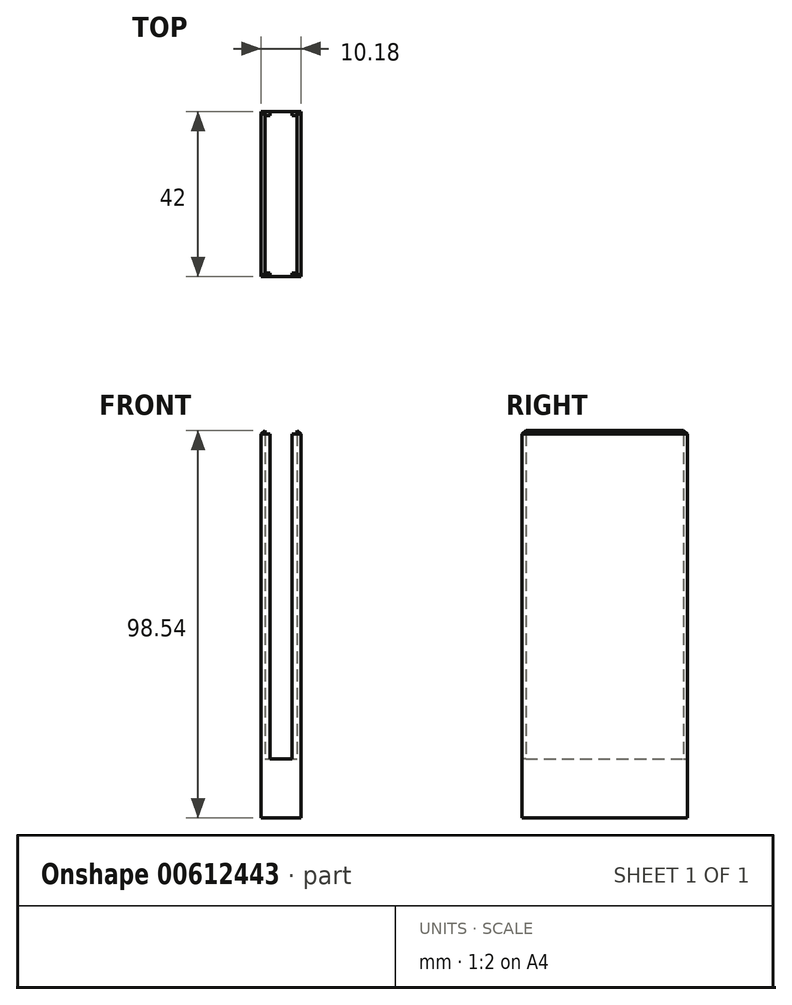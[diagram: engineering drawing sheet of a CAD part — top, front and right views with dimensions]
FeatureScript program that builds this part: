
annotation { "Feature Type Name" : "Feature", "Feature Type Description" : "" }
export const myFeature = defineFeature(function(context is Context, id is Id, definition is map)
    precondition{}
    {
        {
            var Q0;
            Q0=qCreatedBy(makeId("Front.planeOp"),FACE);
            var sketch = newSketch(context, id + "F0", { "sketchPlane" : qUnion([Q0])});
            skLineSegment(sketch, "E0.bottom", {"start": v(-7.86, 55.58) * mm, "end": v(2.32, 55.58) * mm});
            skLineSegment(sketch, "E0.top", {"start": v(-7.86, -44.46) * mm, "end": v(2.32, -44.46) * mm});
            skLineSegment(sketch, "E0.left", {"start": v(-7.86, 55.58) * mm, "end": v(-7.86, -44.46) * mm});
            skLineSegment(sketch, "E0.right", {"start": v(2.32, 55.58) * mm, "end": v(2.32, -44.46) * mm});
            skSolve(sketch);
        }
        {
            var Q0;
            Q0=makeQuery(id+"F0.imprint","IMPRINT",FACE,{"disambiguationData":[TD([[makeQuery(id+"F0.imprint","IMPRINT",EDGE,{"derivedFrom":sQuery(id+"F0.wireOp",EDGE,"E0.bottom")}),-1.0]])]});
            extrude(context, id + "F1", {"entities" : qUnion([Q0]), "depth" : 42 * mm, "offsetDistance" : 25 * mm});
        }
        {
            var Q0;
            Q0=makeQuery(id+"F1.opExtrude","CAP_FACE",FACE,{"disambiguationData":[OSD([sQuery(id+"F0.wireOp",EDGE,"E0.bottom"),sQuery(id+"F0.wireOp",EDGE,"E0.top"),sQuery(id+"F0.wireOp",EDGE,"E0.left"),sQuery(id+"F0.wireOp",EDGE,"E0.right")])],"isStart":false});
            var Q1;
            Q1=makeQuery(id+"F1.opExtrude","CAP_FACE",FACE,{"disambiguationData":[OSD([sQuery(id+"F0.wireOp",EDGE,"E0.bottom"),sQuery(id+"F0.wireOp",EDGE,"E0.top"),sQuery(id+"F0.wireOp",EDGE,"E0.left"),sQuery(id+"F0.wireOp",EDGE,"E0.right")])],"isStart":true});
            shell(context, id + "F2", {"entities" : qUnion([Q0, Q1]), "thickness" : 1 * mm});
        }
        {
            var Q0;
            Q0=makeQuery(id+"F1.opExtrude","SWEPT_FACE",FACE,{"disambiguationData":[OSD([sQuery(id+"F0.wireOp",EDGE,"E0.bottom")])]});
            chamfer(context, id + "F3", {"entities" : qUnion([Q0]), "width" : 2.5 * mm, "tangentPropagation" : true});
        }
        {
            var Q0;
            Q0=makeQuery(id+"F1.opExtrude","CAP_FACE",FACE,{"disambiguationData":[OSD([sQuery(id+"F0.wireOp",EDGE,"E0.bottom"),sQuery(id+"F0.wireOp",EDGE,"E0.top"),sQuery(id+"F0.wireOp",EDGE,"E0.left"),sQuery(id+"F0.wireOp",EDGE,"E0.right")])],"isStart":false});
            var sketch = newSketch(context, id + "F4", { "sketchPlane" : qUnion([Q0])});
            skLineSegment(sketch, "E1.bottom", {"start": v(1.32, -43.46) * mm, "end": v(0, -43.46) * mm});
            skLineSegment(sketch, "E1.top", {"start": v(1.32, 53.08) * mm, "end": v(0, 53.08) * mm});
            skLineSegment(sketch, "E1.left", {"start": v(1.32, -43.46) * mm, "end": v(1.32, 53.08) * mm});
            skLineSegment(sketch, "E1.right", {"start": v(0, -43.46) * mm, "end": v(0, 53.08) * mm});
            skLineSegment(sketch, "E2.bottom", {"start": v(-6.86, 53.08) * mm, "end": v(-5.53, 53.08) * mm});
            skLineSegment(sketch, "E2.top", {"start": v(-6.86, -43.46) * mm, "end": v(-5.53, -43.46) * mm});
            skLineSegment(sketch, "E2.left", {"start": v(-6.86, 53.08) * mm, "end": v(-6.86, -43.46) * mm});
            skLineSegment(sketch, "E2.right", {"start": v(-5.53, 53.08) * mm, "end": v(-5.53, -43.46) * mm});
            skSolve(sketch);
        }
        {
            var Q0;
            Q0=makeQuery(id+"F4.imprint","IMPRINT",FACE,{"disambiguationData":[TD([[makeQuery(id+"F4.imprint","IMPRINT",EDGE,{"derivedFrom":sQuery(id+"F4.wireOp",EDGE,"E1.bottom")}),1.0]])]});
            var Q1;
            Q1=makeQuery(id+"F4.imprint","IMPRINT",FACE,{"disambiguationData":[TD([[makeQuery(id+"F4.imprint","IMPRINT",EDGE,{"derivedFrom":sQuery(id+"F4.wireOp",EDGE,"E2.bottom")}),-1.0]])]});
            extrude(context, id + "F5", {"entities" : qUnion([Q0, Q1]), "operationType" : NewBodyOperationType.ADD, "oppositeDirection" : true, "depth" : 1 * mm, "offsetDistance" : 25 * mm});
        }
        {
            var Q0;
            Q0=makeQuery(id+"F2.opShell","OFFSET_FACE",FACE,{"disambiguationData":[OSD([sQuery(id+"F0.wireOp",EDGE,"E0.top")])]});
            var sketch = newSketch(context, id + "F6", { "sketchPlane" : qUnion([Q0])});
            skLineSegment(sketch, "E3.bottom", {"start": v(-6.86, 0) * mm, "end": v(1.32, 0) * mm});
            skLineSegment(sketch, "E3.top", {"start": v(-6.86, -42.06) * mm, "end": v(1.32, -42.06) * mm});
            skLineSegment(sketch, "E3.left", {"start": v(-6.86, 0) * mm, "end": v(-6.86, -42.06) * mm});
            skLineSegment(sketch, "E3.right", {"start": v(1.32, 0) * mm, "end": v(1.32, -42.06) * mm});
            skSolve(sketch);
        }
        {
            var Q0;
            {var subQ2=sQuery(id+"F6.wireOp",EDGE,"E3.bottom");Q0=makeQuery(id+"F6.imprint","IMPRINT",FACE,{"disambiguationData":[TD([[makeQuery(id+"F6.imprint","IMPRINT",EDGE,{"derivedFrom":subQ2}),-1.0]])]});}
            extrude(context, id + "F7", {"entities" : qUnion([Q0]), "operationType" : NewBodyOperationType.ADD, "depth" : 14 * mm, "offsetDistance" : 25 * mm});
        }
        {
            var Q0;
            Q0=makeQuery(id+"F7.boolean.opBoolean","MERGE",FACE,{"derivedFrom":[makeQuery(id+"F1.opExtrude","CAP_FACE",FACE,{"disambiguationData":[OSD([sQuery(id+"F0.wireOp",EDGE,"E0.bottom"),sQuery(id+"F0.wireOp",EDGE,"E0.top"),sQuery(id+"F0.wireOp",EDGE,"E0.left"),sQuery(id+"F0.wireOp",EDGE,"E0.right")])],"isStart":true}),makeQuery(id+"F7.opExtrude","SWEPT_FACE",FACE,{"disambiguationData":[OSD([sQuery(id+"F6.wireOp",EDGE,"E3.bottom")])]})]});
            var sketch = newSketch(context, id + "F8", { "sketchPlane" : qUnion([Q0])});
            skLineSegment(sketch, "E4.bottom", {"start": v(-1.32, 53.08) * mm, "end": v(0, 53.08) * mm});
            skLineSegment(sketch, "E4.top", {"start": v(-1.32, -29.46) * mm, "end": v(0, -29.46) * mm});
            skLineSegment(sketch, "E4.left", {"start": v(-1.32, 53.08) * mm, "end": v(-1.32, -29.46) * mm});
            skLineSegment(sketch, "E4.right", {"start": v(0, 53.08) * mm, "end": v(0, -29.46) * mm});
            skLineSegment(sketch, "E5.bottom", {"start": v(6.86, -29.46) * mm, "end": v(5.53, -29.46) * mm});
            skLineSegment(sketch, "E5.top", {"start": v(6.86, 53.08) * mm, "end": v(5.53, 53.08) * mm});
            skLineSegment(sketch, "E5.left", {"start": v(6.86, -29.46) * mm, "end": v(6.86, 53.08) * mm});
            skLineSegment(sketch, "E5.right", {"start": v(5.53, -29.46) * mm, "end": v(5.53, 53.08) * mm});
            skSolve(sketch);
        }
        {
            var Q0;
            Q0 = qSketchRegion(id + "F8", true);
            extrude(context, id + "F9", {"entities" : qUnion([Q0]), "operationType" : NewBodyOperationType.ADD, "oppositeDirection" : true, "depth" : 1 * mm, "offsetDistance" : 25 * mm});
        }
    });
